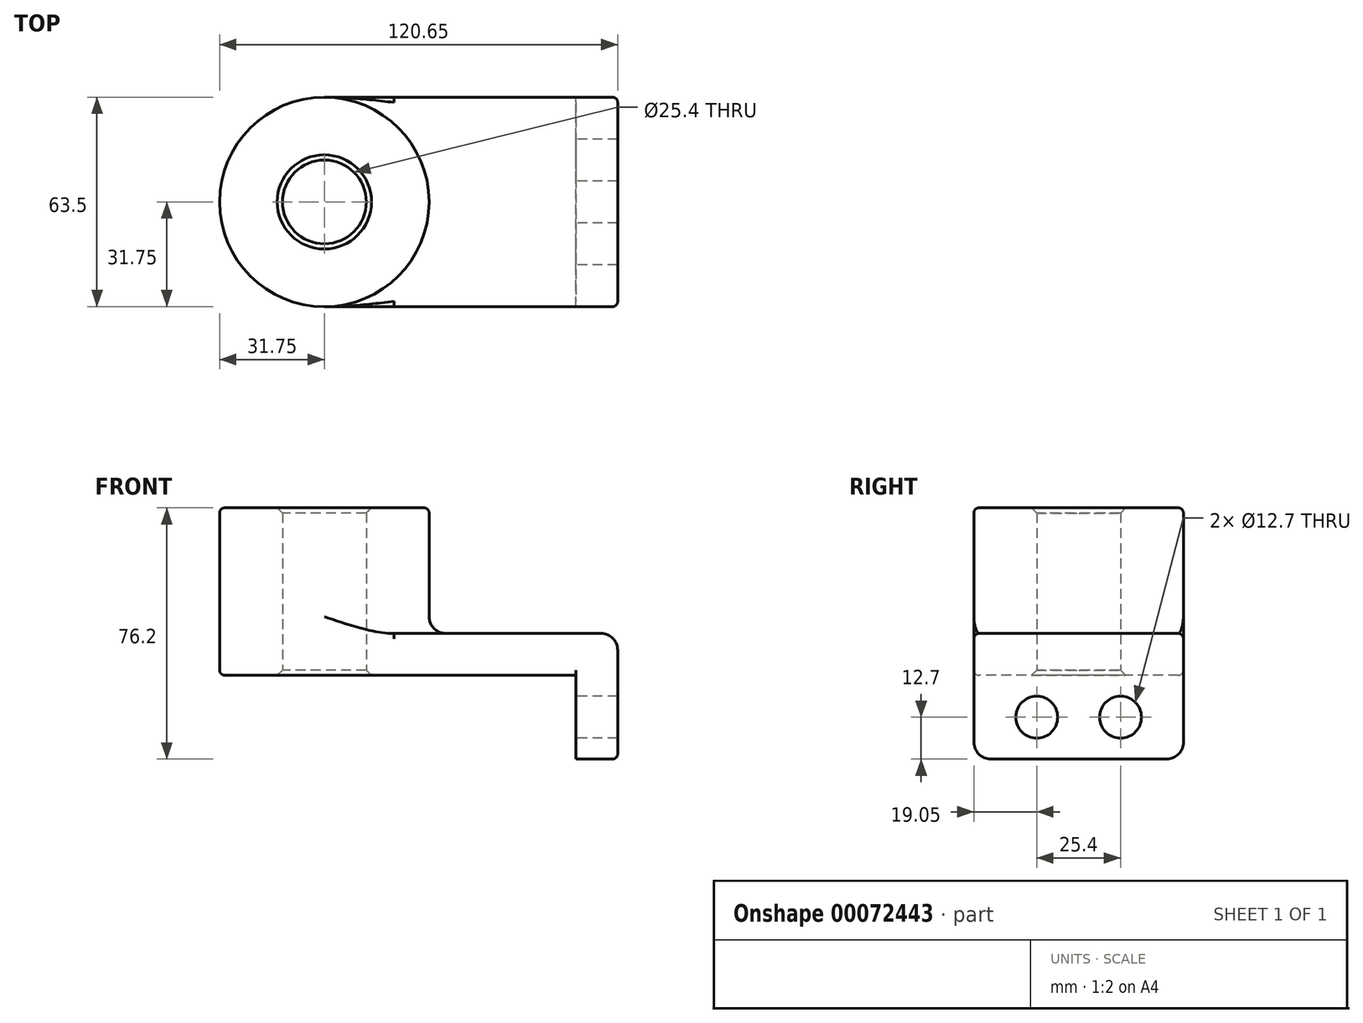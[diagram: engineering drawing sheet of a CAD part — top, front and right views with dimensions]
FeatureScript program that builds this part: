
annotation { "Feature Type Name" : "Feature", "Feature Type Description" : "" }
export const myFeature = defineFeature(function(context is Context, id is Id, definition is map)
    precondition{}
    {
        {
            var Q0;
            Q0=qCreatedBy(makeId("Top.planeOp"),FACE);
            var sketch = newSketch(context, id + "F0", { "sketchPlane" : qUnion([Q0])});
            skLineSegment(sketch, "E0.rect.bottom", {"start": v(-38.1, 31.75) * mm, "end": v(38.1, 31.75) * mm});
            skLineSegment(sketch, "E0.rect.top", {"start": v(-38.1, -31.75) * mm, "end": v(38.1, -31.75) * mm});
            skLineSegment(sketch, "E0.rect.left", {"start": v(-38.1, 31.75) * mm, "end": v(-38.1, -31.75) * mm});
            skLineSegment(sketch, "E0.rect.right", {"start": v(38.1, 31.75) * mm, "end": v(38.1, -31.75) * mm});
            skPoint(sketch, "E0.rect.middle", {"position": v(0, 0) * mm});
            skCircle(sketch, "E1", {"center": v(-38.1, 0) * mm, "radius": 31.75 * mm});
            skCircle(sketch, "E2", {"center": v(-38.1, 0) * mm, "radius": 12.7 * mm});
            skSolve(sketch);
        }
        {
            var Q0;
            Q0 = qSketchRegion(id + "F0", true);
            extrude(context, id + "F1", {"entities" : qUnion([Q0]), "depth" : 12.7 * mm});
        }
        {
            var Q0;
            {var subQ1=sQuery(id+"F0.wireOp",EDGE,"E0.rect.left");var subQ3=sQuery(id+"F0.wireOp",EDGE,"E2");var subQ4=makeQuery(id+"F0.imprint","INTERSECT",VERTEX,{"disambiguationData":[OD(0.0)],"derivedFrom":[subQ1,subQ3]});Q0=makeQuery(id+"F0.imprint","IMPRINT",FACE,{"disambiguationData":[TD([[makeQuery(id+"F0.imprint","IMPRINT",EDGE,{"disambiguationData":[TD([[subQ4,-1.0]])],"derivedFrom":subQ3}),-1.0]])]});}
            var Q1;
            {var subQ1=sQuery(id+"F0.wireOp",EDGE,"E0.rect.left");var subQ3=sQuery(id+"F0.wireOp",EDGE,"E2");var subQ4=makeQuery(id+"F0.imprint","INTERSECT",VERTEX,{"disambiguationData":[OD(0.0)],"derivedFrom":[subQ1,subQ3]});Q1=makeQuery(id+"F0.imprint","IMPRINT",FACE,{"disambiguationData":[TD([[makeQuery(id+"F0.imprint","IMPRINT",EDGE,{"disambiguationData":[TD([[subQ4,1.0]])],"derivedFrom":subQ3}),-1.0]])]});}
            extrude(context, id + "F2", {"entities" : qUnion([Q0, Q1]), "operationType" : NewBodyOperationType.ADD, "depth" : 50.8 * mm});
        }
        {
            var Q0;
            Q0=makeQuery(id+"F1.opExtrude","SWEPT_FACE",FACE,{"disambiguationData":[OSD([sQuery(id+"F0.wireOp",EDGE,"E0.rect.right")])]});
            var sketch = newSketch(context, id + "F3", { "sketchPlane" : qUnion([Q0])});
            skLineSegment(sketch, "E3.bottom", {"start": v(-31.75, 12.7) * mm, "end": v(31.75, 12.7) * mm});
            skLineSegment(sketch, "E3.top", {"start": v(-31.75, -25.4) * mm, "end": v(31.75, -25.4) * mm});
            skLineSegment(sketch, "E3.left", {"start": v(-31.75, 12.7) * mm, "end": v(-31.75, -25.4) * mm});
            skLineSegment(sketch, "E3.right", {"start": v(31.75, 12.7) * mm, "end": v(31.75, -25.4) * mm});
            skLineSegment(sketch, "E4", {"start": v(0, 0) * mm, "end": v(0, -25.4) * mm, "construction": true});
            skCircle(sketch, "E5", {"center": v(-12.7, -12.7) * mm, "radius": 6.35 * mm});
            skCircle(sketch, "E6.MirrorC", {"center": v(12.7, -12.7) * mm, "radius": 6.35 * mm});
            skSolve(sketch);
        }
        {
            var Q0;
            Q0 = qSketchRegion(id + "F3", true);
            extrude(context, id + "F4", {"entities" : qUnion([Q0]), "operationType" : NewBodyOperationType.ADD, "depth" : 12.7 * mm});
        }
        {
            var Q0;
            {var subQ0=sQuery(id+"F0.wireOp",EDGE,"E1");Q0=makeQuery(id+"F2.boolean.opBoolean","INTERSECT",EDGE,{"derivedFrom":[makeQuery(id+"F1.opExtrude","CAP_FACE",FACE,{"disambiguationData":[OSD([sQuery(id+"F0.wireOp",EDGE,"E0.rect.bottom"),sQuery(id+"F0.wireOp",EDGE,"E0.rect.top"),sQuery(id+"F0.wireOp",EDGE,"E0.rect.right"),subQ0,sQuery(id+"F0.wireOp",EDGE,"E2")])],"isStart":false}),makeQuery(id+"F2.opExtrude","SWEPT_FACE",FACE,{"disambiguationData":[OSD([subQ0])]})]});}
            var Q1;
            Q1=makeQuery(id+"F4.opExtrude","CAP_EDGE",EDGE,{"disambiguationData":[OSD([sQuery(id+"F3.wireOp",EDGE,"E3.bottom")])],"isStart":false});
            var Q2;
            Q2=makeQuery(id+"F4.opExtrude","SWEPT_EDGE",EDGE,{"disambiguationData":[OSD([sQuery(id+"F3.wireOp",EDGE,"E3.top"),sQuery(id+"F3.wireOp",EDGE,"E3.left")])]});
            var Q3;
            Q3=makeQuery(id+"F4.opExtrude","SWEPT_EDGE",EDGE,{"disambiguationData":[OSD([sQuery(id+"F3.wireOp",EDGE,"E3.top"),sQuery(id+"F3.wireOp",EDGE,"E3.right")])]});
            fillet(context, id + "F5", {"entities" : qUnion([Q0, Q1, Q2, Q3]), "radius" : 5.08 * mm, "tangentPropagation" : true, "allowEdgeOverflow" : false});
        }
        {
            var Q0;
            Q0=makeQuery(id+"F4.boolean.opBoolean","MERGE",EDGE,{"derivedFrom":[makeQuery(id+"F1.opExtrude","CAP_EDGE",EDGE,{"disambiguationData":[OSD([sQuery(id+"F0.wireOp",EDGE,"E0.rect.top")])],"isStart":false}),makeQuery(id+"F4.opExtrude","SWEPT_EDGE",EDGE,{"disambiguationData":[OSD([sQuery(id+"F3.wireOp",EDGE,"E3.bottom"),sQuery(id+"F3.wireOp",EDGE,"E3.left")])]})]});
            var Q1;
            Q1=makeQuery(id+"F1.opExtrude","CAP_EDGE",EDGE,{"disambiguationData":[OSD([sQuery(id+"F0.wireOp",EDGE,"E0.rect.top")])],"isStart":true});
            var Q2;
            Q2=makeQuery(id+"F1.opExtrude","CAP_EDGE",EDGE,{"disambiguationData":[OSD([sQuery(id+"F0.wireOp",EDGE,"E0.rect.right")])],"isStart":true});
            fillet(context, id + "F6", {"entities" : qUnion([Q0, Q1, Q2]), "radius" : 1.59 * mm, "tangentPropagation" : true, "allowEdgeOverflow" : false});
        }
        {
            var Q0;
            {var subQ0=sQuery(id+"F0.wireOp",EDGE,"E2");Q0=makeQuery(id+"F2.boolean.opBoolean","MERGE",FACE,{"derivedFrom":[makeQuery(id+"F1.opExtrude","SWEPT_FACE",FACE,{"disambiguationData":[OSD([subQ0])]}),makeQuery(id+"F2.opExtrude","SWEPT_FACE",FACE,{"disambiguationData":[OSD([subQ0])]})]});}
            chamfer(context, id + "F7", {"entities" : qUnion([Q0]), "width" : 1.59 * mm, "tangentPropagation" : true});
        }
        {
            var Q0;
            Q0=makeQuery(id+"F2.opExtrude","CAP_EDGE",EDGE,{"disambiguationData":[OSD([sQuery(id+"F0.wireOp",EDGE,"E1")])],"isStart":false});
            fillet(context, id + "F8", {"entities" : qUnion([Q0]), "radius" : 1.59 * mm, "tangentPropagation" : true, "allowEdgeOverflow" : false});
        }
    });
